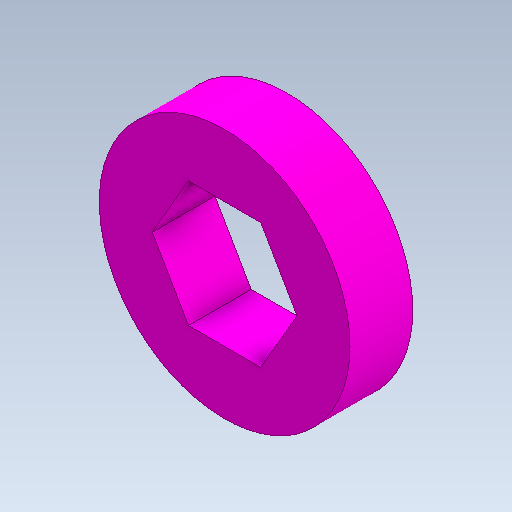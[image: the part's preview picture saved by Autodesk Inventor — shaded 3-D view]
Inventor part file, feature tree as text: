
AUTODESK INVENTOR PART (.ipt)
format: ipt  version: 2021.1 (Build 251245010, 245A)  size: 103,936 bytes
history: native  units: in
note: dims shown in document units (in); Inventor stores cm internally (conversion verified against a paired STEP export)
features: extrude x1, sketch x1
ambient origin geometry x8: Origin, YZ Plane, XZ Plane, XY Plane, X Axis, Y Axis, Z Axis, Center Point
bodies: Solid1 (feature_tree)
feature tree (2):
  extrude  "Extrusion1"  Depth=0.25in
  sketch  "Sketch1"  dims[d0=0.5in d2=1.0in d3=0.2113in d4=0.25in d5=0.0in]
